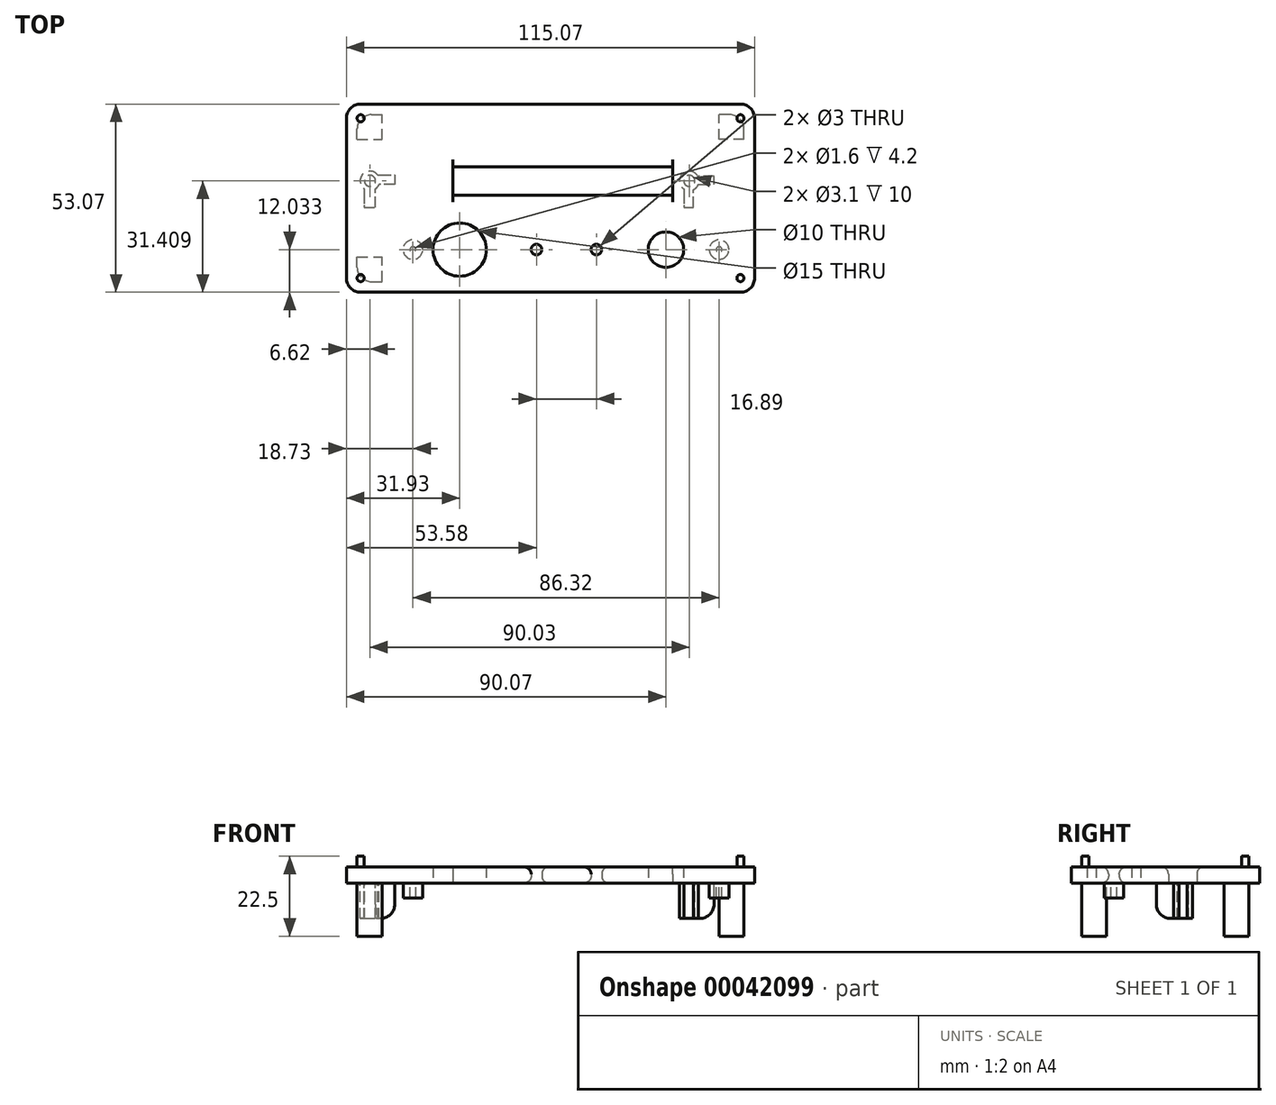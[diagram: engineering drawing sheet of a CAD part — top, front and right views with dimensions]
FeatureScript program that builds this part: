
annotation { "Feature Type Name" : "Feature", "Feature Type Description" : "" }
export const myFeature = defineFeature(function(context is Context, id is Id, definition is map)
    precondition{}
    {
        {
            var Q0;
            Q0=qCreatedBy(makeId("Top.planeOp"),FACE);
            var sketch = newSketch(context, id + "F0", { "sketchPlane" : qUnion([Q0])});
            skLineSegment(sketch, "E0.bottom", {"start": v(-40.47, -4.1) * mm, "end": v(21.53, -4.1) * mm});
            skLineSegment(sketch, "E0.top", {"start": v(-40.47, -12.1) * mm, "end": v(21.53, -12.1) * mm});
            skLineSegment(sketch, "E0.left", {"start": v(-40.47, -4.1) * mm, "end": v(-40.47, -12.1) * mm});
            skLineSegment(sketch, "E0.right", {"start": v(21.53, -4.1) * mm, "end": v(21.53, -12.1) * mm});
            skLineSegment(sketch, "E1.bottom", {"start": v(-70.47, 13.57) * mm, "end": v(44.6, 13.57) * mm});
            skLineSegment(sketch, "E1.left", {"start": v(-70.47, 13.57) * mm, "end": v(-70.47, -39.5) * mm});
            skLineSegment(sketch, "E1.right", {"start": v(44.6, 13.57) * mm, "end": v(44.6, -39.5) * mm});
            skLineSegment(sketch, "E2.top", {"start": v(-70.47, -39.5) * mm, "end": v(44.6, -39.5) * mm});
            skCircle(sketch, "E3", {"center": v(-38.54, -27.47) * mm, "radius": 7.5 * mm});
            skCircle(sketch, "E4", {"center": v(19.6, -27.47) * mm, "radius": 5 * mm});
            skLineSegment(sketch, "E5", {"start": v(-38.54, -27.47) * mm, "end": v(19.6, -27.47) * mm, "construction": true});
            skLineSegment(sketch, "E6", {"start": v(-9.47, -4.1) * mm, "end": v(-9.47, -67.8) * mm, "construction": true});
            skLineSegment(sketch, "E7", {"start": v(-9.47, -27.47) * mm, "end": v(-9.47, -47.05) * mm, "construction": true});
            skCircle(sketch, "E8", {"center": v(-16.89, -27.47) * mm, "radius": 1.5 * mm});
            skCircle(sketch, "E9", {"center": v(0, -27.47) * mm, "radius": 1.5 * mm});
            skSolve(sketch);
        }
        {
            var Q0;
            Q0 = qSketchRegion(id + "F0", true);
            extrude(context, id + "F1", {"entities" : qUnion([Q0]), "depth" : 4.5 * mm});
        }
        {
            var Q0;
            Q0=makeQuery(id+"F1.opExtrude","CAP_FACE",FACE,{"disambiguationData":[OSD([sQuery(id+"F0.wireOp",EDGE,"E0.bottom"),sQuery(id+"F0.wireOp",EDGE,"E0.top"),sQuery(id+"F0.wireOp",EDGE,"E0.left"),sQuery(id+"F0.wireOp",EDGE,"E0.right"),sQuery(id+"F0.wireOp",EDGE,"E1.bottom"),sQuery(id+"F0.wireOp",EDGE,"E1.left"),sQuery(id+"F0.wireOp",EDGE,"E1.right"),sQuery(id+"F0.wireOp",EDGE,"E2.top"),sQuery(id+"F0.wireOp",EDGE,"E3"),sQuery(id+"F0.wireOp",EDGE,"E4"),sQuery(id+"F0.wireOp",EDGE,"E8"),sQuery(id+"F0.wireOp",EDGE,"E9")])],"isStart":true});
            var sketch = newSketch(context, id + "F2", { "sketchPlane" : qUnion([Q0])});
            skCircle(sketch, "E10", {"center": v(-51.74, 27.47) * mm, "radius": 2.75 * mm});
            skCircle(sketch, "E11", {"center": v(-51.74, 27.47) * mm, "radius": 0.8 * mm});
            skLineSegment(sketch, "E12", {"start": v(-38.54, 53.37) * mm, "end": v(-38.54, -15.25) * mm, "construction": true});
            skLineSegment(sketch, "E13", {"start": v(19.6, 54.56) * mm, "end": v(19.6, -16.46) * mm, "construction": true});
            skLineSegment(sketch, "E14", {"start": v(-73.52, 27.47) * mm, "end": v(51.35, 27.47) * mm, "construction": true});
            skPoint(sketch, "E15", {"position": v(-38.54, 27.47) * mm});
            skPoint(sketch, "E16", {"position": v(19.6, 27.47) * mm});
            skCircle(sketch, "E17", {"center": v(34.58, 27.47) * mm, "radius": 0.8 * mm});
            skCircle(sketch, "E18", {"center": v(34.58, 27.47) * mm, "radius": 2.75 * mm});
            skLineSegment(sketch, "E19", {"start": v(-73.6, 8.1) * mm, "end": v(49.99, 8.1) * mm, "construction": true});
            skCircle(sketch, "E20", {"center": v(-63.85, 8.1) * mm, "radius": 1.55 * mm});
            skCircle(sketch, "E21", {"center": v(-63.85, 8.1) * mm, "radius": 2.75 * mm});
            skCircle(sketch, "E22", {"center": v(26.18, 8.1) * mm, "radius": 1.55 * mm});
            skCircle(sketch, "E23", {"center": v(26.18, 8.1) * mm, "radius": 2.75 * mm});
            skPoint(sketch, "E24", {"position": v(-40.47, 8.1) * mm});
            skPoint(sketch, "E25", {"position": v(21.53, 8.1) * mm});
            skLineSegment(sketch, "E26.bottom", {"start": v(-67.47, 36.5) * mm, "end": v(-60.47, 36.5) * mm});
            skLineSegment(sketch, "E26.top", {"start": v(-67.47, 29.5) * mm, "end": v(-60.47, 29.5) * mm});
            skLineSegment(sketch, "E26.left", {"start": v(-67.47, 36.5) * mm, "end": v(-67.47, 29.5) * mm});
            skLineSegment(sketch, "E26.right", {"start": v(-60.47, 36.5) * mm, "end": v(-60.47, 29.5) * mm});
            skLineSegment(sketch, "E27.bottom", {"start": v(-67.47, -3.57) * mm, "end": v(-60.47, -3.57) * mm});
            skLineSegment(sketch, "E27.top", {"start": v(-67.47, -10.57) * mm, "end": v(-60.47, -10.57) * mm});
            skLineSegment(sketch, "E27.left", {"start": v(-67.47, -3.57) * mm, "end": v(-67.47, -10.57) * mm});
            skLineSegment(sketch, "E27.right", {"start": v(-60.47, -3.57) * mm, "end": v(-60.47, -10.57) * mm});
            skLineSegment(sketch, "E28.bottom", {"start": v(41.6, -3.57) * mm, "end": v(34.6, -3.57) * mm});
            skLineSegment(sketch, "E28.top", {"start": v(41.6, -10.57) * mm, "end": v(34.6, -10.57) * mm});
            skLineSegment(sketch, "E28.left", {"start": v(41.6, -3.57) * mm, "end": v(41.6, -10.57) * mm});
            skLineSegment(sketch, "E28.right", {"start": v(34.6, -3.57) * mm, "end": v(34.6, -10.57) * mm});
            skLineSegment(sketch, "E29", {"start": v(-65.43, 10.34) * mm, "end": v(-65.51, 15.5) * mm});
            skLineSegment(sketch, "E30", {"start": v(-65.51, 15.5) * mm, "end": v(-62.29, 15.5) * mm});
            skLineSegment(sketch, "E31", {"start": v(-62.29, 15.5) * mm, "end": v(-62.29, 10.35) * mm});
            skLineSegment(sketch, "E32", {"start": v(-61.64, 6.46) * mm, "end": v(-56.85, 6.46) * mm});
            skLineSegment(sketch, "E33", {"start": v(-56.85, 6.46) * mm, "end": v(-56.85, 9.13) * mm});
            skLineSegment(sketch, "E34", {"start": v(-56.85, 9.13) * mm, "end": v(-61.3, 9.13) * mm});
            skLineSegment(sketch, "E35", {"start": v(24.62, 10.35) * mm, "end": v(24.62, 15.5) * mm});
            skPoint(sketch, "E35.endSnap0", {"position": v(-63.9, 15.5) * mm});
            skLineSegment(sketch, "E36", {"start": v(24.62, 15.5) * mm, "end": v(27.31, 15.5) * mm});
            skLineSegment(sketch, "E37", {"start": v(27.31, 15.5) * mm, "end": v(27.31, 10.6) * mm});
            skLineSegment(sketch, "E38", {"start": v(28.73, 9.13) * mm, "end": v(33.17, 9.13) * mm});
            skLineSegment(sketch, "E39", {"start": v(33.17, 9.13) * mm, "end": v(33.17, 6.83) * mm});
            skLineSegment(sketch, "E40", {"start": v(33.17, 6.83) * mm, "end": v(28.62, 6.83) * mm});
            skSolve(sketch);
        }
        {
            var Q0;
            Q0=makeQuery(id+"F2.imprint","IMPRINT",FACE,{"disambiguationData":[TD([[makeQuery(id+"F2.imprint","IMPRINT",EDGE,{"derivedFrom":sQuery(id+"F2.wireOp",EDGE,"E10")}),1.0]])]});
            var Q1;
            Q1=makeQuery(id+"F2.imprint","IMPRINT",FACE,{"disambiguationData":[TD([[makeQuery(id+"F2.imprint","IMPRINT",EDGE,{"derivedFrom":sQuery(id+"F2.wireOp",EDGE,"E17")}),-1.0]])]});
            extrude(context, id + "F3", {"entities" : qUnion([Q0, Q1]), "operationType" : NewBodyOperationType.ADD, "depth" : 4.2 * mm});
        }
        {
            var Q0;
            Q0=makeQuery(id+"F2.imprint","IMPRINT",FACE,{"disambiguationData":[TD([[makeQuery(id+"F2.imprint","IMPRINT",EDGE,{"derivedFrom":sQuery(id+"F2.wireOp",EDGE,"E20")}),-1.0]])]});
            var Q1;
            Q1=makeQuery(id+"F2.imprint","IMPRINT",FACE,{"disambiguationData":[TD([[makeQuery(id+"F2.imprint","IMPRINT",EDGE,{"derivedFrom":sQuery(id+"F2.wireOp",EDGE,"E22")}),-1.0]])]});
            var Q2;
            {var subQ0=sQuery(id+"F2.wireOp",EDGE,"E29");Q2=makeQuery(id+"F2.imprint","IMPRINT",FACE,{"disambiguationData":[TD([[makeQuery(id+"F2.imprint","IMPRINT",EDGE,{"derivedFrom":subQ0}),-1.0]])]});}
            var Q3;
            {var subQ1=sQuery(id+"F2.wireOp",EDGE,"E32");Q3=makeQuery(id+"F2.imprint","IMPRINT",FACE,{"disambiguationData":[TD([[makeQuery(id+"F2.imprint","IMPRINT",EDGE,{"derivedFrom":subQ1}),1.0]])]});}
            var Q4;
            {var subQ1=sQuery(id+"F2.wireOp",EDGE,"E35");Q4=makeQuery(id+"F2.imprint","IMPRINT",FACE,{"disambiguationData":[TD([[makeQuery(id+"F2.imprint","IMPRINT",EDGE,{"derivedFrom":subQ1}),-1.0]])]});}
            var Q5;
            {var subQ1=sQuery(id+"F2.wireOp",EDGE,"E38");Q5=makeQuery(id+"F2.imprint","IMPRINT",FACE,{"disambiguationData":[TD([[makeQuery(id+"F2.imprint","IMPRINT",EDGE,{"derivedFrom":subQ1}),-1.0]])]});}
            extrude(context, id + "F4", {"entities" : qUnion([Q0, Q1, Q2, Q3, Q4, Q5]), "operationType" : NewBodyOperationType.ADD, "depth" : 10 * mm});
        }
        {
            var Q0;
            Q0=makeQuery(id+"F2.imprint","IMPRINT",FACE,{"disambiguationData":[TD([[makeQuery(id+"F2.imprint","IMPRINT",EDGE,{"derivedFrom":sQuery(id+"F2.wireOp",EDGE,"E26.bottom")}),-1.0]])]});
            var Q1;
            Q1=makeQuery(id+"F2.imprint","IMPRINT",FACE,{"disambiguationData":[TD([[makeQuery(id+"F2.imprint","IMPRINT",EDGE,{"derivedFrom":sQuery(id+"F2.wireOp",EDGE,"E28.bottom")}),1.0]])]});
            var Q2;
            Q2=makeQuery(id+"F2.imprint","IMPRINT",FACE,{"disambiguationData":[TD([[makeQuery(id+"F2.imprint","IMPRINT",EDGE,{"derivedFrom":sQuery(id+"F2.wireOp",EDGE,"E27.bottom")}),-1.0]])]});
            extrude(context, id + "F5", {"entities" : qUnion([Q0, Q1, Q2]), "operationType" : NewBodyOperationType.ADD, "depth" : 15 * mm});
        }
        {
            var Q0;
            Q0=makeQuery(id+"F1.opExtrude","SWEPT_EDGE",EDGE,{"disambiguationData":[OSD([sQuery(id+"F0.wireOp",EDGE,"E1.left"),sQuery(id+"F0.wireOp",EDGE,"E2.top")])]});
            var Q1;
            Q1=makeQuery(id+"F1.opExtrude","SWEPT_EDGE",EDGE,{"disambiguationData":[OSD([sQuery(id+"F0.wireOp",EDGE,"E1.bottom"),sQuery(id+"F0.wireOp",EDGE,"E1.left")])]});
            var Q2;
            Q2=makeQuery(id+"F5.opExtrude","SWEPT_EDGE",EDGE,{"disambiguationData":[OSD([sQuery(id+"F2.wireOp",EDGE,"E26.bottom"),sQuery(id+"F2.wireOp",EDGE,"E26.left")])]});
            var Q3;
            Q3=makeQuery(id+"F5.opExtrude","SWEPT_EDGE",EDGE,{"disambiguationData":[OSD([sQuery(id+"F2.wireOp",EDGE,"E27.top"),sQuery(id+"F2.wireOp",EDGE,"E27.left")])]});
            var Q4;
            Q4=makeQuery(id+"F5.opExtrude","SWEPT_EDGE",EDGE,{"disambiguationData":[OSD([sQuery(id+"F2.wireOp",EDGE,"E28.top"),sQuery(id+"F2.wireOp",EDGE,"E28.left")])]});
            var Q5;
            Q5=makeQuery(id+"F1.opExtrude","SWEPT_EDGE",EDGE,{"disambiguationData":[OSD([sQuery(id+"F0.wireOp",EDGE,"E1.bottom"),sQuery(id+"F0.wireOp",EDGE,"E1.right")])]});
            var Q6;
            Q6=makeQuery(id+"F1.opExtrude","SWEPT_EDGE",EDGE,{"disambiguationData":[OSD([sQuery(id+"F0.wireOp",EDGE,"E1.right"),sQuery(id+"F0.wireOp",EDGE,"E2.top")])]});
            var Q7;
            Q7=makeQuery(id+"F4.opExtrude","CAP_EDGE",EDGE,{"disambiguationData":[OSD([sQuery(id+"F2.wireOp",EDGE,"E30")])],"isStart":true});
            var Q8;
            Q8=makeQuery(id+"F4.opExtrude","CAP_EDGE",EDGE,{"disambiguationData":[OSD([sQuery(id+"F2.wireOp",EDGE,"E33")])],"isStart":true});
            var Q9;
            Q9=makeQuery(id+"F4.opExtrude","CAP_EDGE",EDGE,{"disambiguationData":[OSD([sQuery(id+"F2.wireOp",EDGE,"E30")])],"isStart":false});
            var Q10;
            Q10=makeQuery(id+"F4.opExtrude","CAP_EDGE",EDGE,{"disambiguationData":[OSD([sQuery(id+"F2.wireOp",EDGE,"E33")])],"isStart":false});
            var Q11;
            Q11=makeQuery(id+"F4.opExtrude","CAP_EDGE",EDGE,{"disambiguationData":[OSD([sQuery(id+"F2.wireOp",EDGE,"E36")])],"isStart":false});
            var Q12;
            Q12=makeQuery(id+"F4.opExtrude","CAP_EDGE",EDGE,{"disambiguationData":[OSD([sQuery(id+"F2.wireOp",EDGE,"E36")])],"isStart":true});
            var Q13;
            Q13=makeQuery(id+"F4.opExtrude","CAP_EDGE",EDGE,{"disambiguationData":[OSD([sQuery(id+"F2.wireOp",EDGE,"E39")])],"isStart":false});
            var Q14;
            Q14=makeQuery(id+"F4.opExtrude","CAP_EDGE",EDGE,{"disambiguationData":[OSD([sQuery(id+"F2.wireOp",EDGE,"E39")])],"isStart":true});
            fillet(context, id + "F6", {"entities" : qUnion([Q0, Q1, Q2, Q3, Q4, Q5, Q6, Q7, Q8, Q9, Q10, Q11, Q12, Q13, Q14]), "radius" : 4 * mm, "tangentPropagation" : true, "allowEdgeOverflow" : false});
        }
        {
            var Q0;
            Q0=makeQuery(id+"F3.opExtrude","CAP_EDGE",EDGE,{"disambiguationData":[OSD([sQuery(id+"F2.wireOp",EDGE,"E18")])],"isStart":true});
            var Q1;
            Q1=makeQuery(id+"F3.opExtrude","CAP_EDGE",EDGE,{"disambiguationData":[OSD([sQuery(id+"F2.wireOp",EDGE,"E10")])],"isStart":true});
            var Q2;
            Q2=makeQuery(id+"F5.opExtrude","CAP_EDGE",EDGE,{"disambiguationData":[OSD([sQuery(id+"F2.wireOp",EDGE,"E27.right")])],"isStart":true});
            var Q3;
            Q3=makeQuery(id+"F5.opExtrude","CAP_EDGE",EDGE,{"disambiguationData":[OSD([sQuery(id+"F2.wireOp",EDGE,"E27.bottom")])],"isStart":true});
            var Q4;
            Q4=makeQuery(id+"F5.opExtrude","CAP_EDGE",EDGE,{"disambiguationData":[OSD([sQuery(id+"F2.wireOp",EDGE,"E28.right")])],"isStart":true});
            var Q5;
            Q5=makeQuery(id+"F5.opExtrude","CAP_EDGE",EDGE,{"disambiguationData":[OSD([sQuery(id+"F2.wireOp",EDGE,"E28.bottom")])],"isStart":true});
            var Q6;
            Q6=makeQuery(id+"F5.opExtrude","CAP_EDGE",EDGE,{"disambiguationData":[OSD([sQuery(id+"F2.wireOp",EDGE,"E26.right")])],"isStart":true});
            var Q7;
            Q7=makeQuery(id+"F5.opExtrude","CAP_EDGE",EDGE,{"disambiguationData":[OSD([sQuery(id+"F2.wireOp",EDGE,"E26.top")])],"isStart":true});
            var Q8;
            Q8=makeQuery(id+"F1.opExtrude","CAP_EDGE",EDGE,{"disambiguationData":[OSD([sQuery(id+"F0.wireOp",EDGE,"E0.top")])],"isStart":false});
            var Q9;
            Q9=makeQuery(id+"F1.opExtrude","CAP_EDGE",EDGE,{"disambiguationData":[OSD([sQuery(id+"F0.wireOp",EDGE,"E0.bottom")])],"isStart":false});
            var Q10;
            Q10=makeQuery(id+"F1.opExtrude","CAP_EDGE",EDGE,{"disambiguationData":[OSD([sQuery(id+"F0.wireOp",EDGE,"E9")])],"isStart":false});
            var Q11;
            Q11=makeQuery(id+"F1.opExtrude","CAP_EDGE",EDGE,{"disambiguationData":[OSD([sQuery(id+"F0.wireOp",EDGE,"E8")])],"isStart":false});
            var Q12;
            Q12=makeQuery(id+"F1.opExtrude","CAP_EDGE",EDGE,{"disambiguationData":[OSD([sQuery(id+"F0.wireOp",EDGE,"E9")])],"isStart":true});
            var Q13;
            Q13=makeQuery(id+"F1.opExtrude","CAP_EDGE",EDGE,{"disambiguationData":[OSD([sQuery(id+"F0.wireOp",EDGE,"E8")])],"isStart":true});
            fillet(context, id + "F7", {"entities" : qUnion([Q0, Q1, Q2, Q3, Q4, Q5, Q6, Q7, Q8, Q9, Q10, Q11, Q12, Q13]), "radius" : 2 * mm, "tangentPropagation" : true, "allowEdgeOverflow" : false});
        }
        {
            var Q0;
            Q0=makeQuery(id+"F1.opExtrude","CAP_FACE",FACE,{"disambiguationData":[OSD([sQuery(id+"F0.wireOp",EDGE,"E0.bottom"),sQuery(id+"F0.wireOp",EDGE,"E0.top"),sQuery(id+"F0.wireOp",EDGE,"E0.left"),sQuery(id+"F0.wireOp",EDGE,"E0.right"),sQuery(id+"F0.wireOp",EDGE,"E1.bottom"),sQuery(id+"F0.wireOp",EDGE,"E1.left"),sQuery(id+"F0.wireOp",EDGE,"E1.right"),sQuery(id+"F0.wireOp",EDGE,"E2.top"),sQuery(id+"F0.wireOp",EDGE,"E3"),sQuery(id+"F0.wireOp",EDGE,"E4"),sQuery(id+"F0.wireOp",EDGE,"E8"),sQuery(id+"F0.wireOp",EDGE,"E9")])],"isStart":false});
            var sketch = newSketch(context, id + "F8", { "sketchPlane" : qUnion([Q0])});
            skCircle(sketch, "E41", {"center": v(-66.47, 9.57) * mm, "radius": 1 * mm});
            skCircle(sketch, "E42", {"center": v(40.6, 9.57) * mm, "radius": 1 * mm});
            skCircle(sketch, "E43", {"center": v(40.6, -35.5) * mm, "radius": 1 * mm});
            skCircle(sketch, "E44", {"center": v(-66.47, -35.5) * mm, "radius": 1 * mm});
            skSolve(sketch);
        }
        {
            var Q0;
            Q0 = qSketchRegion(id + "F8", true);
            extrude(context, id + "F9", {"entities" : qUnion([Q0]), "operationType" : NewBodyOperationType.ADD, "depth" : 3 * mm});
        }
    });
